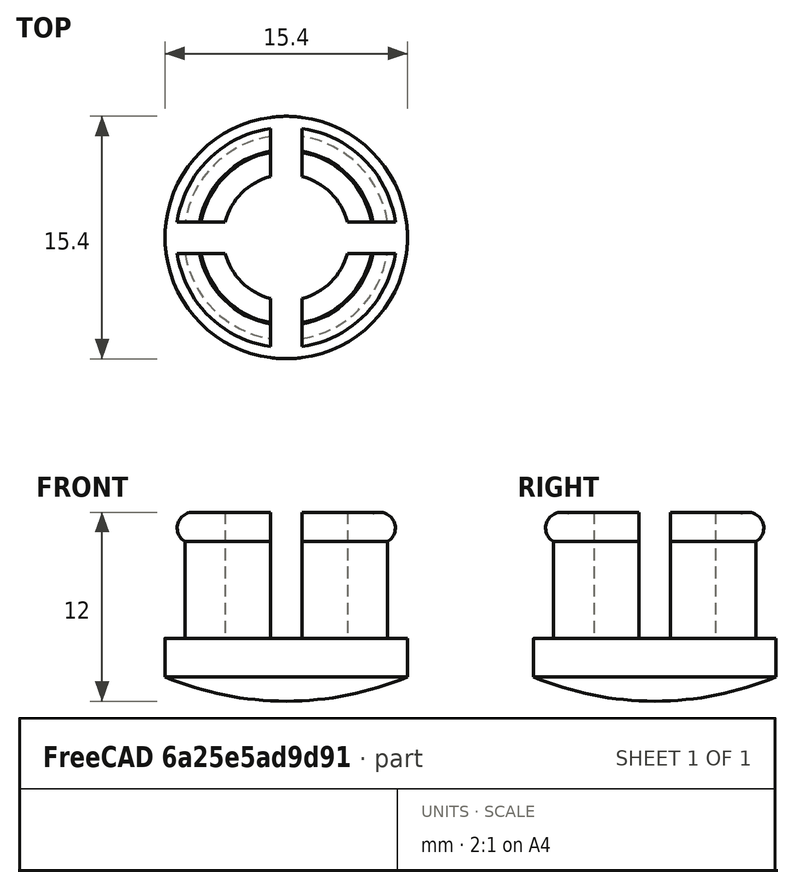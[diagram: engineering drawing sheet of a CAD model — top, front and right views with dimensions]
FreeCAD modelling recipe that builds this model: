
FCSTD DOCUMENT  (FreeCAD 0.22R38465 (Git))
Label: Stopica
License: All rights reserved
LicenseURL: https://en.wikipedia.org/wiki/All_rights_reserved
objects: Part::Cylinder×3, Part::MultiFuse×3, Part::Box×2, Part::Sphere×1, Part::MultiCommon×1, Part::Torus×1, Part::Chamfer×1, Part::Cut×1
note: 13 computed .brp shape members not serialized (recipe doc carries the construction recipe); baked Part::Feature solids carry a one-line shape summary decoded from their .brp

FEATURE [Part::Cylinder] Cylinder
  Angle = 360
  AttacherType = Attacher::AttachEngine3D
  FirstAngle = 0
  Height = 4
  Radius = 7.7
  SecondAngle = 0
FEATURE [Part::Sphere] Sphere
  Angle1 = -90
  Angle2 = 90
  Angle3 = 360
  AttacherType = Attacher::AttachEngine3D
  Placement = pos=(0,0,20) rot=(0,0,1;0rad)
  Radius = 20
FEATURE [Part::MultiCommon] Common
  Refine = true
  Shapes = -> [Sphere,Cylinder]
FEATURE [Part::Cylinder] Cylinder001
  Angle = 360
  AttacherType = Attacher::AttachEngine3D
  FirstAngle = 0
  Height = 10
  Placement = pos=(0,0,2) rot=(0,0,1;0rad)
  Radius = 6.5
  SecondAngle = 0
FEATURE [Part::MultiFuse] Fusion  label="Stopica"
  Refine = true
  Shapes = -> [Common,Cylinder001]
FEATURE [Part::Torus] Torus
  Angle1 = -180
  Angle2 = 180
  Angle3 = 360
  AttacherType = Attacher::AttachEngine3D
  Placement = pos=(0,0,11) rot=(0,0,1;0rad)
  Radius1 = 6
  Radius2 = 1
FEATURE [Part::Chamfer] Chamfer
  Base = -> Fusion
  EdgeLinks = -> Fusion [Edge3]
  Edges = 1 edges r=1: [Edge3]
FEATURE [Part::MultiFuse] Fusion001
  Refine = true
  Shapes = -> [Chamfer,Torus]
FEATURE [Part::Box] Box  label="Cube"
  AttacherType = Attacher::AttachEngine3D
  Height = 10
  Length = 2
  Placement = pos=(-1,-10,4) rot=(0,0,1;0rad)
  Width = 20
FEATURE [Part::Box] Box001  label="Cube001"
  AttacherType = Attacher::AttachEngine3D
  Height = 10
  Length = 20
  Placement = pos=(-10,-1,4) rot=(0,0,1;0rad)
  Width = 2
FEATURE [Part::Cylinder] Cylinder002
  Angle = 360
  AttacherType = Attacher::AttachEngine3D
  FirstAngle = 0
  Height = 10
  Placement = pos=(0,0,4) rot=(0,0,1;0rad)
  Radius = 4
  SecondAngle = 0
FEATURE [Part::MultiFuse] Fusion002
  Refine = true
  Shapes = -> [Cylinder002,Box001,Box]
FEATURE [Part::Cut] Cut  label="Stopa1"
  Base = -> Fusion001
  Refine = true
  Tool = -> Fusion002
